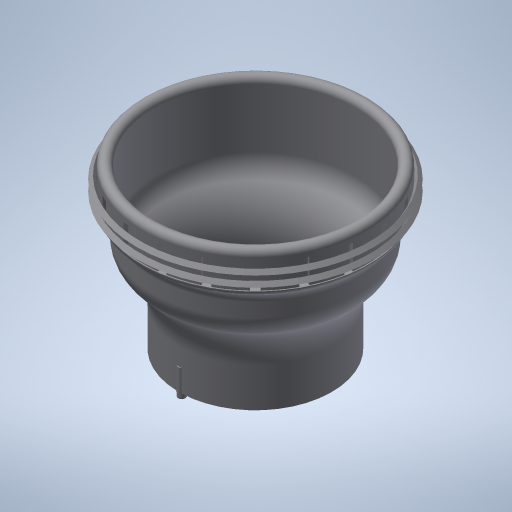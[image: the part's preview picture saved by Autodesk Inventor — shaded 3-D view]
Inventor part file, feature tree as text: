
AUTODESK INVENTOR PART (.ipt)
format: ipt  version: 2023.3 (Build 273359000, 359)  size: 1,411,072 bytes
history: native  units: mm
features: other x9, boolean_combine x2, revolve x1, sketch x1
ambient origin geometry x8: Origin, YZ Plane, XZ Plane, XY Plane, X Axis, Y Axis, Z Axis, Center Point
bodies: Solid4 (feature_tree), Solid1 (feature_tree), Solid3 (feature_tree)
feature tree (13):
  other  "Sealing_ring_20x1_silicone_h.ipt"
  other  "Mold_1_Sealing_ring_20x1_silicone_x.ipt"
  other  "Mold_2_Sealing_ring_20x1_silicone_h.ipt"
  boolean_combine  "Combine1"
  revolve  "Revolution1"  [1 undecoded]
  boolean_combine  "Combine2"
  other  "Solid1::Sealing_ring_20x1_silicone_h.ipt"
  other  "TaggingFeature1"
  other  "Solid1::Mold_1_Sealing_ring_20x1_silicone_x.ipt"
  other  "TaggingFeature2"
  other  "Solid3::Mold_2_Sealing_ring_20x1_silicone_h.ipt"
  other  "TaggingFeature3"
  sketch  "Sketch1"  dims[d0=10.0mm d1=10.0mm d2=10.0mm d3=360.0deg d4=0.872665mm d5=0.872665mm]
note: 1 required parameter value undecoded (feature->parameter linkage not recoverable at this tier; creation-order binding heuristic only, values carry confidence <= 0.55)
